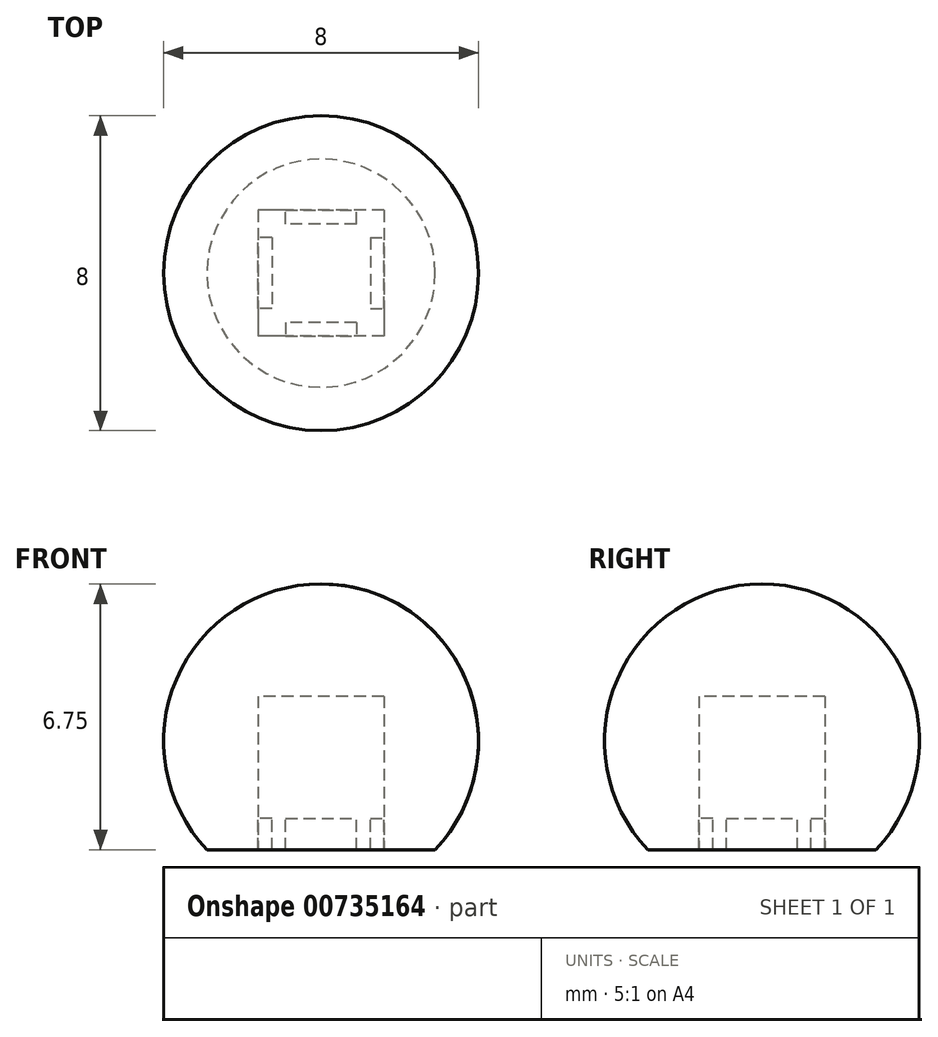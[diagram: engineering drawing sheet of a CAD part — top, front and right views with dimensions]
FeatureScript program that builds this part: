
annotation { "Feature Type Name" : "Feature", "Feature Type Description" : "" }
export const myFeature = defineFeature(function(context is Context, id is Id, definition is map)
    precondition{}
    {
        {
            var Q0;
            Q0=qCreatedBy(makeId("Front.planeOp"),FACE);
            var sketch = newSketch(context, id + "F0", { "sketchPlane" : qUnion([Q0])});
            skLineSegment(sketch, "E0", {"start": v(0, 0) * mm, "end": v(2.9, 0) * mm});
            skArc(sketch, "E1", {"start": v(2.9, 0) * mm, "mid": v(3.68, 4.33) * mm, "end": v(0, 6.75) * mm});
            skLineSegment(sketch, "E2", {"start": v(0, 6.75) * mm, "end": v(-0.9, 6.75) * mm, "construction": true});
            skLineSegment(sketch, "E3", {"start": v(0, 6.75) * mm, "end": v(0, 0) * mm});
            skSolve(sketch);
        }
        {
            var Q0;
            Q0 = qSketchRegion(id + "F0", true);
            var Q1;
            Q1=sQuery(id+"F0.wireOp",EDGE,"E3");
            revolve(context, id + "F1", {"surfaceOperationType" : NewSurfaceOperationType.NEW, "entities" : qUnion([Q0]), "axis" : qUnion([Q1]), "revolveType" : RevolveType.FULL});
        }
        {
            var Q0;
            Q0=makeQuery(id+"F1.opRevolve","SWEPT_FACE",FACE,{"disambiguationData":[OSD([sQuery(id+"F0.wireOp",EDGE,"E0")])]});
            var sketch = newSketch(context, id + "F2", { "sketchPlane" : qUnion([Q0])});
            skLineSegment(sketch, "E4.bottom", {"start": v(1.6, -1.6) * mm, "end": v(-1.6, -1.6) * mm});
            skLineSegment(sketch, "E4.top", {"start": v(1.6, 1.6) * mm, "end": v(-1.6, 1.6) * mm});
            skLineSegment(sketch, "E4.left", {"start": v(1.6, -1.6) * mm, "end": v(1.6, 1.6) * mm});
            skLineSegment(sketch, "E4.right", {"start": v(-1.6, -1.6) * mm, "end": v(-1.6, 1.6) * mm});
            skPoint(sketch, "E4.middle", {"position": v(0, 0) * mm});
            skSolve(sketch);
        }
        {
            var Q0;
            Q0=makeQuery(id+"F2.imprint","IMPRINT",FACE,{"disambiguationData":[TD([[makeQuery(id+"F2.imprint","IMPRINT",EDGE,{"derivedFrom":sQuery(id+"F2.wireOp",EDGE,"E4.bottom")}),-1.0]])]});
            extrude(context, id + "F3", {"entities" : qUnion([Q0]), "operationType" : NewBodyOperationType.REMOVE, "oppositeDirection" : true, "depth" : 3.9 * mm, "offsetDistance" : 25 * mm});
        }
        {
            var Q0;
            Q0=makeQuery(id+"F3.boolean.opBoolean","COPY",FACE,{"derivedFrom":makeQuery(id+"F3.opExtrude","SWEPT_FACE",FACE,{"disambiguationData":[OSD([sQuery(id+"F2.wireOp",EDGE,"E4.top")])]})});
            var sketch = newSketch(context, id + "F4", { "sketchPlane" : qUnion([Q0])});
            skLineSegment(sketch, "E5.bottom", {"start": v(0.9, 0) * mm, "end": v(-0.9, 0) * mm});
            skLineSegment(sketch, "E5.top", {"start": v(0.9, 0.8) * mm, "end": v(-0.9, 0.8) * mm});
            skLineSegment(sketch, "E5.left", {"start": v(0.9, 0) * mm, "end": v(0.9, 0.8) * mm});
            skLineSegment(sketch, "E5.right", {"start": v(-0.9, 0) * mm, "end": v(-0.9, 0.8) * mm});
            skSolve(sketch);
        }
        {
            var Q0;
            Q0=makeQuery(id+"F4.imprint","IMPRINT",FACE,{"disambiguationData":[TD([[makeQuery(id+"F4.imprint","IMPRINT",EDGE,{"derivedFrom":sQuery(id+"F4.wireOp",EDGE,"E5.bottom")}),1.0]])]});
            extrude(context, id + "F5", {"entities" : qUnion([Q0]), "operationType" : NewBodyOperationType.ADD, "depth" : 0.35 * mm, "offsetDistance" : 25 * mm});
        }
        {
            var Q0;
            Q0=makeQuery(id+"F3.boolean.opBoolean","COPY",FACE,{"derivedFrom":makeQuery(id+"F3.opExtrude","SWEPT_FACE",FACE,{"disambiguationData":[OSD([sQuery(id+"F2.wireOp",EDGE,"E4.bottom")])]})});
            var sketch = newSketch(context, id + "F6", { "sketchPlane" : qUnion([Q0])});
            skLineSegment(sketch, "E6.0", {"start": v(-0.9, 0.8) * mm, "end": v(0.9, 0.8) * mm});
            skLineSegment(sketch, "E6.1", {"start": v(-0.9, 0) * mm, "end": v(-0.9, 0.8) * mm});
            skLineSegment(sketch, "E6.2", {"start": v(0.9, 0) * mm, "end": v(0.9, 0.8) * mm});
            skLineSegment(sketch, "E6.3", {"start": v(-0.9, 0) * mm, "end": v(0.9, 0) * mm});
            skSolve(sketch);
        }
        {
            var Q0;
            Q0 = qSketchRegion(id + "F6", true);
            extrude(context, id + "F7", {"entities" : qUnion([Q0]), "operationType" : NewBodyOperationType.ADD, "depth" : 0.35 * mm, "offsetDistance" : 25 * mm});
        }
        {
            var Q0;
            Q0=makeQuery(id+"F3.boolean.opBoolean","COPY",FACE,{"derivedFrom":makeQuery(id+"F3.opExtrude","SWEPT_FACE",FACE,{"disambiguationData":[OSD([sQuery(id+"F2.wireOp",EDGE,"E4.left")])]})});
            var sketch = newSketch(context, id + "F8", { "sketchPlane" : qUnion([Q0])});
            skLineSegment(sketch, "E7.bottom", {"start": v(0.9, 0) * mm, "end": v(-0.9, 0) * mm});
            skLineSegment(sketch, "E7.top", {"start": v(0.9, 0.8) * mm, "end": v(-0.9, 0.8) * mm});
            skLineSegment(sketch, "E7.left", {"start": v(0.9, 0) * mm, "end": v(0.9, 0.8) * mm});
            skLineSegment(sketch, "E7.right", {"start": v(-0.9, 0) * mm, "end": v(-0.9, 0.8) * mm});
            skSolve(sketch);
        }
        {
            var Q0;
            Q0 = qSketchRegion(id + "F8", true);
            extrude(context, id + "F9", {"entities" : qUnion([Q0]), "operationType" : NewBodyOperationType.ADD, "depth" : 0.35 * mm, "offsetDistance" : 25 * mm});
        }
        {
            var Q0;
            Q0=makeQuery(id+"F3.boolean.opBoolean","COPY",FACE,{"derivedFrom":makeQuery(id+"F3.opExtrude","SWEPT_FACE",FACE,{"disambiguationData":[OSD([sQuery(id+"F2.wireOp",EDGE,"E4.right")])]})});
            var sketch = newSketch(context, id + "F10", { "sketchPlane" : qUnion([Q0])});
            skLineSegment(sketch, "E8.0", {"start": v(-0.9, 0) * mm, "end": v(-0.9, 0.8) * mm});
            skLineSegment(sketch, "E9.0", {"start": v(-0.9, 0) * mm, "end": v(0.9, 0) * mm});
            skLineSegment(sketch, "E10.0", {"start": v(0.9, 0) * mm, "end": v(0.9, 0.8) * mm});
            skLineSegment(sketch, "E11.0", {"start": v(-0.9, 0.8) * mm, "end": v(0.9, 0.8) * mm});
            skSolve(sketch);
        }
        {
            var Q0;
            Q0 = qSketchRegion(id + "F10", true);
            extrude(context, id + "F11", {"entities" : qUnion([Q0]), "operationType" : NewBodyOperationType.ADD, "depth" : 0.35 * mm, "offsetDistance" : 25 * mm});
        }
    });
